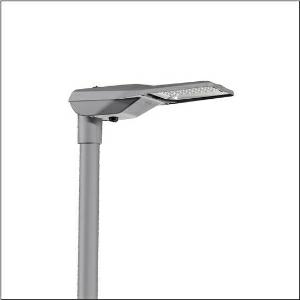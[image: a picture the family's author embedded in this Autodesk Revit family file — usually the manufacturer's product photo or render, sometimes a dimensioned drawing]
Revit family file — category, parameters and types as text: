
# Revit family: streetlight_sl_21_mini___st1_0ab_5xe2m33t08gb_59c5
name_source: partatom
category: Lighting Fixtures
units: mm (PartAtom-declared; Revit-internal decimal feet)

## family parameters
Cut with Voids When Loaded = No
Host = Face
Light Source = No
Part Type = Normal
Room Calculation Point = No
Round Connector Dimension = Use Diameter
Shared = No

## types (1)
- --- (1 x LED, 5230 lm, 40.4 W, 3000K)
    Apparent Load = 40 VA
    CIE Flux Codes = 38 73 97 100 100
    Color Rendering = 70
    Color Temperature = 3000K
    Default Elevation = 1800 mm
    Description = Streetlight SL 21 mini, mast luminaire, primary light control with lens, of PMMA, primary optical cover: cover, of toughened safety glass, transparent, light distribution: ST1.0aB, light emission: direct distribution, primary light characteristic: asymmetric, installation type: side-entry, post-top, LED, High Power LED, rated luminous flux: 5.230lm, luminous efficacy: 130lm/W, light colour: 730, colour temperature: 3000K, control gear: D4i, control: flexible luminous flux parameterisation, time-dependent luminous flux control, constant luminous flux control, overheat protection, pre-setting: logarithmic dimming characteristic, mains connection: 220..240V, AC, 50/60Hz, start of lifetime: 40W, end of service life: 41W, reduction: 19W, luminaire housing, of diecast aluminium, powder-coated, SITECO metallic grey (DB 702S), corrosivity category C5 high according to DIN EN ISO 12944, please order mast flange separately, inclination adjustable: 0°, 5°, 10°, 15°, sealing non-destructively replaceable, multi-level sealing system, length: 628mm, width: 235mm, height: 110mm, mast flange for spigot size: 42mm (side-entry): 5XC10008XM4, 60/48mm (side-entry/post-top): 5XC10108XM2, 76/60mm (side-entry/post-top): 5XC10108XM1, mounting height: 4..8m, Smart Interface below and above, protection rating (complete): IP66, insulation class (complete): insulation class II (safety insulation), certification: CE, ENEC, ENEC+, VDE, impact resistance: IK10, permissible operating ambient temperature for outdoor applications: -40..+50°C, standard-compliant lighting for roads and squares, packaging unit: 1 piece

Light Distribution: ST1.0aB
    Height = 110 mm
    Lamp = 1 x LED
    Lamp Light Flux = 5230 lm
    Lamp Power = 40.4 W
    Lamp count = 1
    Length = 625 mm
    Luminous efficacy = 129 lm/W
    Manufacturer = Siteco
    ModVariant = No
    Model = 5XE2M33T08GB
    Number of Poles = 1
    OnlyDefault = Yes
    Power Factor = 1
    Product Name = Streetlight SL 21 mini | ST1.0aB
    Product group = mast luminaire | pylon top
    ProductGroupID = 6100
    Protection Class = Protection class II
    Protection Degree = IP 66
    RLX_Detail_Level = 1
    RLX_Emergency_Light_Flux = 0 lm
    RLX_Emergency_Type = 0
    RLX_Emergency_Type_DB = No
    RlxData = <blob elided: 26397 chars, md5=a3319e19>
    Socket = socket
    Standby Power = 0 W
    System Light Flux = 5230 lm
    System Power = 40 W
    Type Comments = factory setting: luminous flux: 100 % | dim-lin: 254 | 812 mA
    Type Image = l_1003514.jpg
    URL = http://relux.com
    VarID = @adj_180007
    Voltage = 0 V
    Weight = 0.00 kg
    Width = 234 mm

## geometry (parser evidence)
native form markers: Blend x4, Sweep x13
no freeform markers — native parametric forms only
